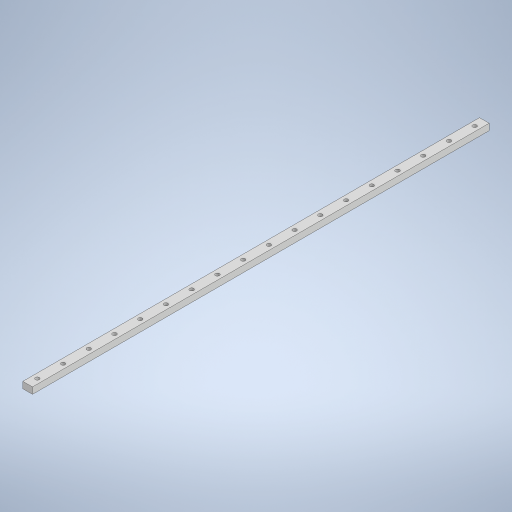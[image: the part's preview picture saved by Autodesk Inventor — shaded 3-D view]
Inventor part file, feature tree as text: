
AUTODESK INVENTOR PART (.ipt)
format: ipt  version: 2023 (Build 270158000, 158)  size: 284,672 bytes
history: native  units: mm
features: sketch x2, extrude x1, plane x1, revolve x1, pattern_linear x1
ambient origin geometry x8: Origin, YZ Plane, XZ Plane, XY Plane, X Axis, Y Axis, Z Axis, Center Point
bodies: Solid1 (feature_tree)
feature tree (6):
  extrude  "Extrusion1"  Depth=10.0mm
  plane  "Work Plane1"
  revolve  "Revolution1"  [1 undecoded]
  pattern_linear  "Rectangular Pattern1"  Spacing1=6.0mm  [1 undecoded]
  sketch  "Sketch1"  dims[d0=15.0mm d1=10.0mm]
  sketch  "Sketch4"  dims[d2=710.0mm d3=0.0mm d5=-7.5mm d6=6.0mm d7=3.5mm d8=4.5mm d9=15.0mm d10=360.0deg d11=200.0mm d13=40.0mm]
note: 2 required parameter values undecoded (feature->parameter linkage not recoverable at this tier; creation-order binding heuristic only, values carry confidence <= 0.55)